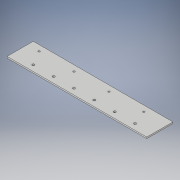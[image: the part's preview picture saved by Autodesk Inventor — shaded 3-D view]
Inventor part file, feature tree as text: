
AUTODESK INVENTOR PART (.ipt)
format: ipt  version: 2019 (Build 230136000, 136)  size: 137,728 bytes
history: native  units: in
note: dims shown in document units (in); Inventor stores cm internally (conversion verified against a paired STEP export)
features: sketch x3, hole x2, extrude x1
ambient origin geometry x8: Origin, YZ Plane, XZ Plane, XY Plane, X Axis, Y Axis, Z Axis, Center Point
bodies: Solid1 (feature_tree)
feature tree (6):
  extrude  "Extrusion1"  Depth=2.25in
  hole  "Hole1"  [1 undecoded]
  hole  "Hole2"  [1 undecoded]
  sketch  "Sketch1"  dims[d0=12.0in d1=2.25in]
  sketch  "Sketch2"  dims[d2=0.125in d3=0.0in d8=1.75in]
  sketch  "Sketch3"  dims[d9=1.75in d10=1.75in d11=1.75in d12=1.75in d13=1.75in d14=1.0in d15=3.0in d16=3.0in d17=3.0in d18=0.201in d19=0.75in d20=0.385in d21=0.25in d22=0.5635in d23=1.0in d24=0.8108in d25=1.75in d26=1.75in d27=1.75in d28=1.75in d29=1.75in d30=1.75in d31=1.0in d32=3.0in d33=3.0in d34=3.0in d35=0.15in d36=0.75in d37=0.279in d38=0.25in d39=0.5635in d40=1.0in d41=0.8108in]
note: 2 required parameter values undecoded (feature->parameter linkage not recoverable at this tier; creation-order binding heuristic only, values carry confidence <= 0.55)
